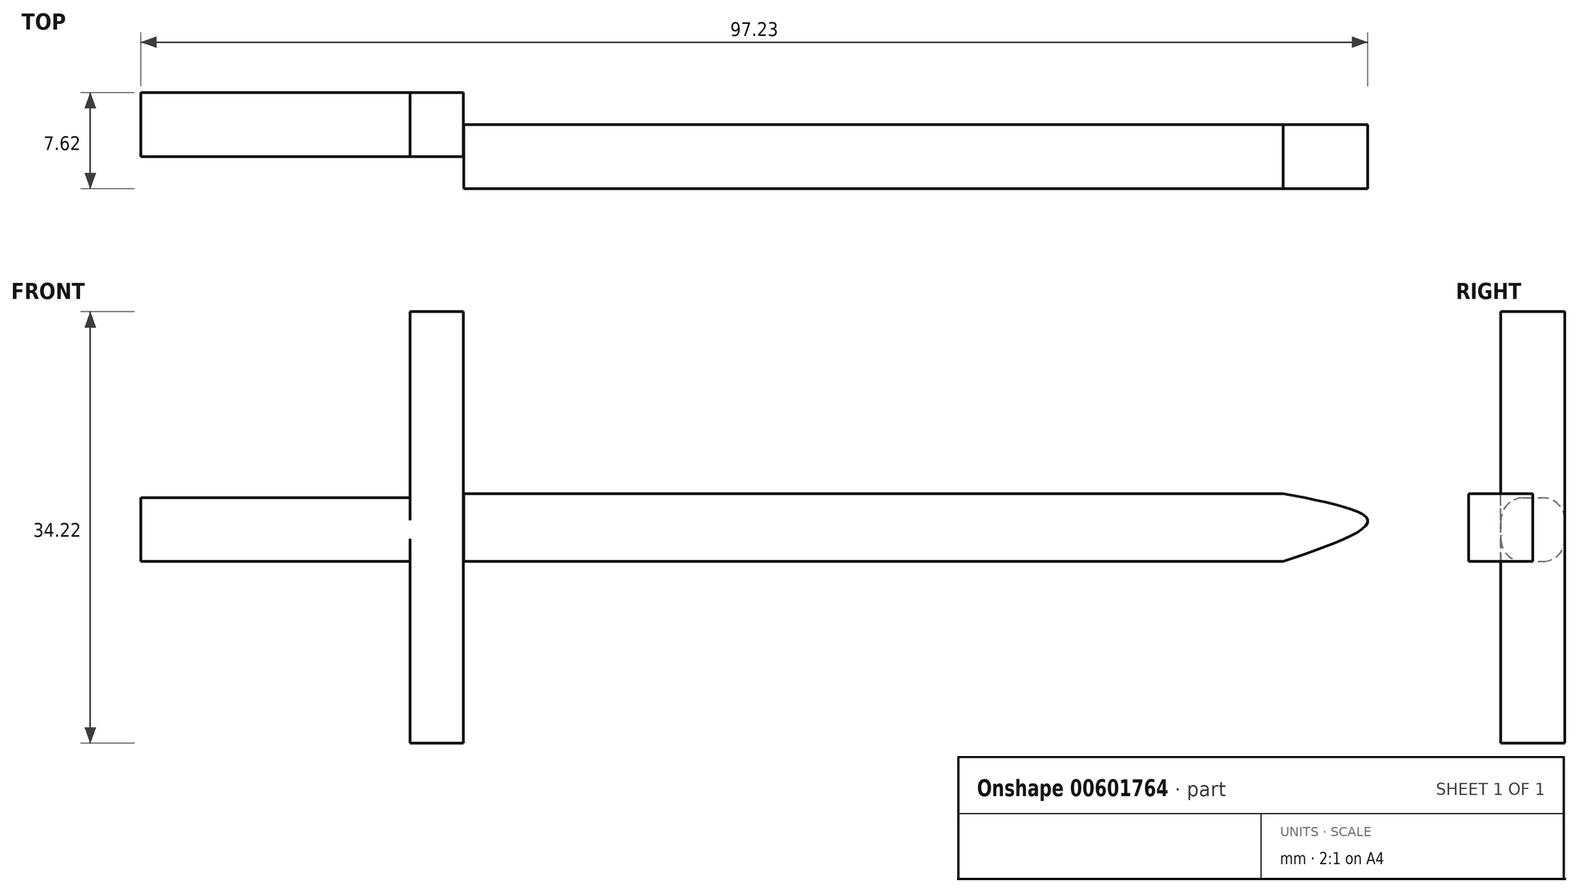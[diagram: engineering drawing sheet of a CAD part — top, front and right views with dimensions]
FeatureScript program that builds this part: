
annotation { "Feature Type Name" : "Feature", "Feature Type Description" : "" }
export const myFeature = defineFeature(function(context is Context, id is Id, definition is map)
    precondition{}
    {
        {
            var Q0;
            Q0=qCreatedBy(makeId("Front.planeOp"),FACE);
            var sketch = newSketch(context, id + "F0", { "sketchPlane" : qUnion([Q0])});
            skLineSegment(sketch, "E0.bottom", {"start": v(-64.05, 5.05) * mm, "end": v(-42.72, 5.05) * mm});
            skLineSegment(sketch, "E0.top", {"start": v(-64.05, 0) * mm, "end": v(-42.72, 0) * mm});
            skLineSegment(sketch, "E0.left", {"start": v(-64.05, 5.05) * mm, "end": v(-64.05, 0) * mm});
            skLineSegment(sketch, "E0.right", {"start": v(-42.72, 5.05) * mm, "end": v(-42.72, 0) * mm});
            skLineSegment(sketch, "E1.bottom", {"start": v(-42.72, 5.05) * mm, "end": v(-38.5, 5.05) * mm});
            skLineSegment(sketch, "E1.top", {"start": v(-42.72, 19.82) * mm, "end": v(-38.5, 19.82) * mm});
            skLineSegment(sketch, "E1.left", {"start": v(-42.72, 5.05) * mm, "end": v(-42.72, 19.82) * mm});
            skLineSegment(sketch, "E1.right", {"start": v(-38.5, 5.05) * mm, "end": v(-38.5, 19.82) * mm});
            skPoint(sketch, "E2.oppositeSnap0", {"position": v(-38.5, 12.44) * mm});
            skLineSegment(sketch, "E2.bottom", {"start": v(-42.72, 0) * mm, "end": v(-38.5, 0) * mm});
            skLineSegment(sketch, "E2.top", {"start": v(-42.72, -14.4) * mm, "end": v(-38.5, -14.4) * mm});
            skLineSegment(sketch, "E2.left", {"start": v(-42.72, 0) * mm, "end": v(-42.72, -14.4) * mm});
            skLineSegment(sketch, "E2.right", {"start": v(-38.5, 0) * mm, "end": v(-38.5, -14.4) * mm});
            skLineSegment(sketch, "E3.left", {"start": v(-42.72, 0) * mm, "end": v(-42.72, 5.05) * mm});
            skLineSegment(sketch, "E4", {"start": v(-38.5, 5.05) * mm, "end": v(-38.5, 0) * mm});
            skSolve(sketch);
        }
        {
            var Q0;
            Q0=makeQuery(id+"F0.imprint","IMPRINT",FACE,{"disambiguationData":[TD([[makeQuery(id+"F0.imprint","IMPRINT",EDGE,{"derivedFrom":sQuery(id+"F0.wireOp",EDGE,"E1.bottom")}),1.0]])]});
            var Q1;
            Q1=makeQuery(id+"F0.imprint","IMPRINT",FACE,{"disambiguationData":[TD([[makeQuery(id+"F0.imprint","IMPRINT",EDGE,{"derivedFrom":sQuery(id+"F0.wireOp",EDGE,"E2.bottom")}),-1.0]])]});
            var Q2;
            Q2=makeQuery(id+"F0.imprint","IMPRINT",FACE,{"disambiguationData":[TD([[makeQuery(id+"F0.imprint","IMPRINT",EDGE,{"derivedFrom":sQuery(id+"F0.wireOp",EDGE,"E1.bottom")}),-1.0]])]});
            var Q3;
            Q3=makeQuery(id+"F0.imprint","IMPRINT",FACE,{"disambiguationData":[TD([[makeQuery(id+"F0.imprint","IMPRINT",EDGE,{"derivedFrom":sQuery(id+"F0.wireOp",EDGE,"E0.bottom")}),-1.0]])]});
            extrude(context, id + "F1", {"entities" : qUnion([Q0, Q1, Q2, Q3]), "endBound" : BoundingType.SYMMETRIC, "depth" : 5.08 * mm, "offsetDistance" : 25.4 * mm});
        }
        {
            var Q0;
            Q0=makeQuery(id+"F1.opExtrude","CAP_EDGE",EDGE,{"disambiguationData":[OSD([sQuery(id+"F0.wireOp",EDGE,"E0.bottom")])],"isStart":false});
            var Q1;
            Q1=makeQuery(id+"F1.opExtrude","CAP_EDGE",EDGE,{"disambiguationData":[OSD([sQuery(id+"F0.wireOp",EDGE,"E0.top")])],"isStart":true});
            var Q2;
            Q2=makeQuery(id+"F1.opExtrude","CAP_EDGE",EDGE,{"disambiguationData":[OSD([sQuery(id+"F0.wireOp",EDGE,"E0.bottom")])],"isStart":true});
            var Q3;
            Q3=makeQuery(id+"F1.opExtrude","CAP_EDGE",EDGE,{"disambiguationData":[OSD([sQuery(id+"F0.wireOp",EDGE,"E0.top")])],"isStart":false});
            fillet(context, id + "F2", {"entities" : qUnion([Q0, Q1, Q2, Q3]), "radius" : 1.78 * mm, "tangentPropagation" : true, "allowEdgeOverflow" : false});
        }
        {
            var Q0;
            Q0=qCreatedBy(makeId("Front.planeOp"),FACE);
            var sketch = newSketch(context, id + "F3", { "sketchPlane" : qUnion([Q0])});
            skLineSegment(sketch, "E5.bottom", {"start": v(-38.45, 5.39) * mm, "end": v(26.47, 5.39) * mm});
            skLineSegment(sketch, "E5.top", {"start": v(-38.45, 0) * mm, "end": v(26.47, 0) * mm});
            skLineSegment(sketch, "E5.left", {"start": v(-38.45, 5.39) * mm, "end": v(-38.45, 0) * mm});
            skLineSegment(sketch, "E5.right", {"start": v(26.47, 5.39) * mm, "end": v(26.47, 0) * mm});
            skFitSpline(sketch, "E6", {"points": [v(26.47, 5.39) * mm, v(33.18, 3.23) * mm, v(26.47, 0) * mm], "startDerivative": vector(20.22, -3.88) * mm, "endDerivative": vector(-20.03, -6.89) * mm});
            skSolve(sketch);
        }
        {
            var Q0;
            Q0=makeQuery(id+"F3.imprint","IMPRINT",FACE,{"disambiguationData":[TD([[makeQuery(id+"F3.imprint","IMPRINT",EDGE,{"derivedFrom":sQuery(id+"F3.wireOp",EDGE,"E5.bottom")}),-1.0]])]});
            var Q1;
            Q1=makeQuery(id+"F3.imprint","IMPRINT",FACE,{"disambiguationData":[TD([[makeQuery(id+"F3.imprint","IMPRINT",EDGE,{"derivedFrom":sQuery(id+"F3.wireOp",EDGE,"E5.right")}),1.0]])]});
            extrude(context, id + "F4", {"entities" : qUnion([Q0, Q1]), "depth" : 5.08 * mm, "offsetDistance" : 25.4 * mm});
        }
    });
